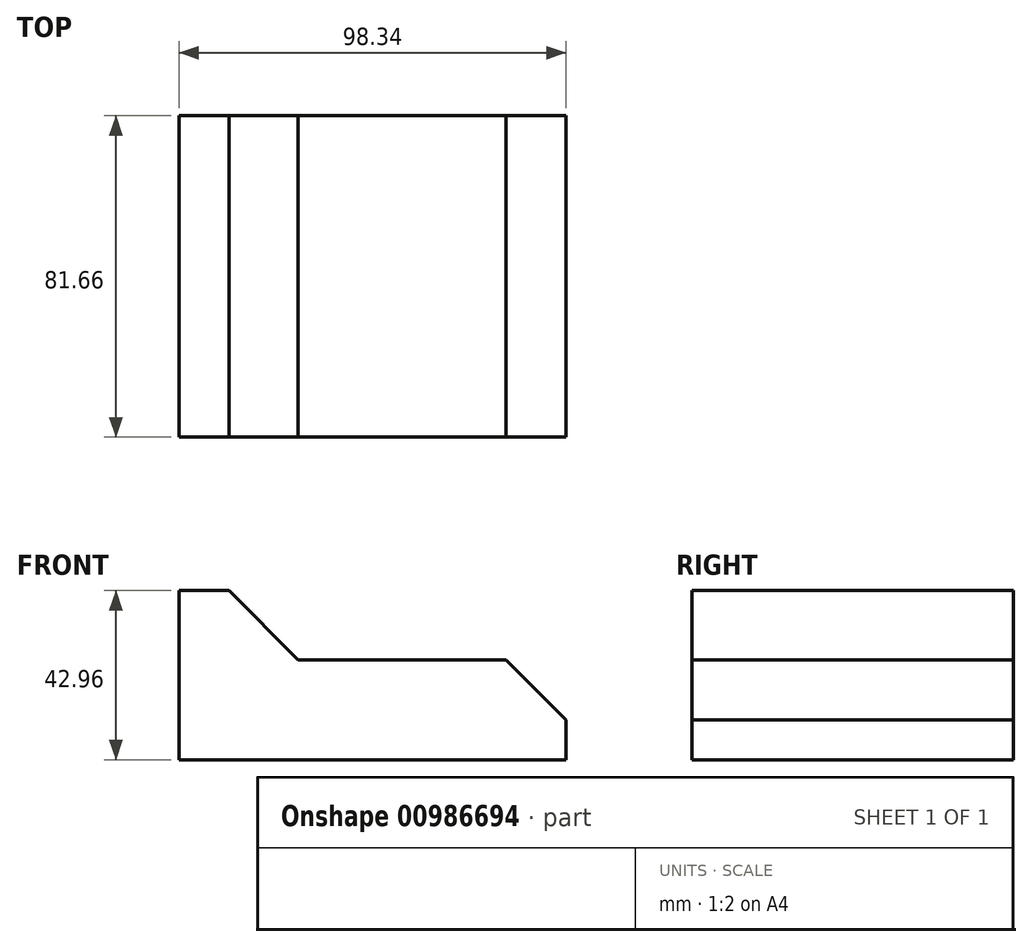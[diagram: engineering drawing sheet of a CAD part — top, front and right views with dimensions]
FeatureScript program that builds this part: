
annotation { "Feature Type Name" : "Feature", "Feature Type Description" : "" }
export const myFeature = defineFeature(function(context is Context, id is Id, definition is map)
    precondition{}
    {
        {
            var Q0;
            Q0=qCreatedBy(makeId("Top.planeOp"),FACE);
            var sketch = newSketch(context, id + "F0", { "sketchPlane" : qUnion([Q0])});
            skLineSegment(sketch, "E0.bottom", {"start": v(0, -23.3) * mm, "end": v(41.38, -23.3) * mm});
            skLineSegment(sketch, "E0.top", {"start": v(0, 20.26) * mm, "end": v(41.38, 20.26) * mm});
            skLineSegment(sketch, "E0.left", {"start": v(0, -23.3) * mm, "end": v(0, 20.26) * mm});
            skLineSegment(sketch, "E0.right", {"start": v(41.38, -23.3) * mm, "end": v(41.38, 20.26) * mm});
            skLineSegment(sketch, "E1.bottom", {"start": v(41.38, 20.26) * mm, "end": v(70.31, 20.26) * mm});
            skLineSegment(sketch, "E1.top", {"start": v(41.38, -23.3) * mm, "end": v(70.31, -23.3) * mm});
            skLineSegment(sketch, "E1.left", {"start": v(41.38, 20.26) * mm, "end": v(41.38, -23.3) * mm});
            skLineSegment(sketch, "E1.right", {"start": v(70.31, 20.26) * mm, "end": v(70.31, -23.3) * mm});
            skLineSegment(sketch, "E2.bottom", {"start": v(0, 20.26) * mm, "end": v(-15.33, 20.26) * mm});
            skLineSegment(sketch, "E2.top", {"start": v(0, -23.3) * mm, "end": v(-15.33, -23.3) * mm});
            skLineSegment(sketch, "E2.left", {"start": v(0, 20.26) * mm, "end": v(0, -23.3) * mm});
            skLineSegment(sketch, "E2.right", {"start": v(-15.33, 20.26) * mm, "end": v(-15.33, -23.3) * mm});
            skSolve(sketch);
        }
        {
            var Q0;
            Q0=makeQuery(id+"F0.imprint","IMPRINT",FACE,{"disambiguationData":[TD([[makeQuery(id+"F0.imprint","IMPRINT",EDGE,{"derivedFrom":sQuery(id+"F0.wireOp",EDGE,"E2.bottom")}),1.0]])]});
            var Q1;
            Q1=makeQuery(id+"F0.imprint","IMPRINT",FACE,{"disambiguationData":[TD([[makeQuery(id+"F0.imprint","IMPRINT",EDGE,{"derivedFrom":sQuery(id+"F0.wireOp",EDGE,"E0.bottom")}),1.0]])]});
            var Q2;
            Q2=makeQuery(id+"F0.imprint","IMPRINT",FACE,{"disambiguationData":[TD([[makeQuery(id+"F0.imprint","IMPRINT",EDGE,{"derivedFrom":sQuery(id+"F0.wireOp",EDGE,"E1.bottom")}),-1.0]])]});
            extrude(context, id + "F1", {"entities" : qUnion([Q0, Q1, Q2]), "depth" : 25.4 * mm, "offsetDistance" : 25.4 * mm});
        }
        {
            var Q0;
            Q0=makeQuery(id+"F1.opExtrude","CAP_FACE",FACE,{"disambiguationData":[OSD([sQuery(id+"F0.wireOp",EDGE,"E0.bottom"),sQuery(id+"F0.wireOp",EDGE,"E0.top"),sQuery(id+"F0.wireOp",EDGE,"E1.bottom"),sQuery(id+"F0.wireOp",EDGE,"E1.top"),sQuery(id+"F0.wireOp",EDGE,"E1.right"),sQuery(id+"F0.wireOp",EDGE,"E2.bottom"),sQuery(id+"F0.wireOp",EDGE,"E2.top"),sQuery(id+"F0.wireOp",EDGE,"E2.right")])],"isStart":false});
            var sketch = newSketch(context, id + "F2", { "sketchPlane" : qUnion([Q0])});
            skLineSegment(sketch, "E3.bottom", {"start": v(-15.33, 20.26) * mm, "end": v(2.23, 20.26) * mm});
            skLineSegment(sketch, "E3.top", {"start": v(-15.33, -23.3) * mm, "end": v(2.23, -23.3) * mm});
            skLineSegment(sketch, "E3.left", {"start": v(-15.33, 20.26) * mm, "end": v(-15.33, -23.3) * mm});
            skLineSegment(sketch, "E3.right", {"start": v(2.23, 20.26) * mm, "end": v(2.23, -23.3) * mm});
            skLineSegment(sketch, "E4.bottom", {"start": v(51.88, 20.26) * mm, "end": v(70.31, 20.26) * mm});
            skLineSegment(sketch, "E4.top", {"start": v(51.88, -23.3) * mm, "end": v(70.31, -23.3) * mm});
            skLineSegment(sketch, "E4.left", {"start": v(51.88, 20.26) * mm, "end": v(51.88, -23.3) * mm});
            skLineSegment(sketch, "E4.right", {"start": v(70.31, 20.26) * mm, "end": v(70.31, -23.3) * mm});
            skSolve(sketch);
        }
        {
            var Q0;
            Q0=makeQuery(id+"F2.imprint","IMPRINT",FACE,{"disambiguationData":[TD([[makeQuery(id+"F2.imprint","IMPRINT",EDGE,{"derivedFrom":sQuery(id+"F2.wireOp",EDGE,"E3.bottom")}),1.0]])]});
            extrude(context, id + "F3", {"entities" : qUnion([Q0]), "operationType" : NewBodyOperationType.ADD, "depth" : 25.4 * mm, "offsetDistance" : 25.4 * mm});
        }
        {
            var Q0;
            Q0=makeQuery(id+"F1.opExtrude","CAP_EDGE",EDGE,{"disambiguationData":[OSD([sQuery(id+"F0.wireOp",EDGE,"E1.right")])],"isStart":false});
            chamfer(context, id + "F4", {"entities" : qUnion([Q0]), "width" : 15.24 * mm, "tangentPropagation" : true});
        }
        {
            var Q0;
            Q0=makeQuery(id+"F3.opExtrude","CAP_EDGE",EDGE,{"disambiguationData":[OSD([sQuery(id+"F2.wireOp",EDGE,"E3.right")])],"isStart":false});
            chamfer(context, id + "F5", {"entities" : qUnion([Q0]), "width" : 25.4 * mm, "tangentPropagation" : true});
        }
        {
            var Q0;
            Q0=makeQuery(id+"F3.boolean.opBoolean","MERGE",FACE,{"derivedFrom":[makeQuery(id+"F1.opExtrude","SWEPT_FACE",FACE,{"disambiguationData":[OSD([sQuery(id+"F0.wireOp",EDGE,"E2.right")])]}),makeQuery(id+"F3.opExtrude","SWEPT_FACE",FACE,{"disambiguationData":[OSD([sQuery(id+"F2.wireOp",EDGE,"E3.left")])]})]});
            extrude(context, id + "F6", {"entities" : qUnion([Q0]), "operationType" : NewBodyOperationType.ADD, "depth" : 12.7 * mm, "offsetDistance" : 25.4 * mm});
        }
        {
            var Q0;
            {var subQ0=sQuery(id+"F2.wireOp",EDGE,"E3.bottom");var subQ1=sQuery(id+"F0.wireOp",EDGE,"E2.bottom");Q0=makeQuery(id+"F6.boolean.opBoolean","MERGE",FACE,{"derivedFrom":[makeQuery(id+"F3.boolean.opBoolean","MERGE",FACE,{"derivedFrom":[makeQuery(id+"F1.opExtrude","SWEPT_FACE",FACE,{"disambiguationData":[OSD([sQuery(id+"F0.wireOp",EDGE,"E0.top"),sQuery(id+"F0.wireOp",EDGE,"E1.bottom"),subQ1])]}),makeQuery(id+"F3.opExtrude","SWEPT_FACE",FACE,{"disambiguationData":[OSD([subQ0])]})]}),makeQuery(id+"F6.opExtrude","SWEPT_FACE",FACE,{"disambiguationData":[OSD([subQ1,sQuery(id+"F0.wireOp",EDGE,"E2.right"),subQ0,sQuery(id+"F2.wireOp",EDGE,"E3.left")])]})]});}
            extrude(context, id + "F7", {"entities" : qUnion([Q0]), "operationType" : NewBodyOperationType.ADD, "depth" : 25.4 * mm, "offsetDistance" : 25.4 * mm});
        }
        {
            var Q0;
            Q0=makeQuery(id+"F7.opExtrude","CAP_FACE",FACE,{"disambiguationData":[OSD([sQuery(id+"F0.wireOp",EDGE,"E0.top"),sQuery(id+"F0.wireOp",EDGE,"E1.bottom"),sQuery(id+"F0.wireOp",EDGE,"E2.bottom"),sQuery(id+"F0.wireOp",EDGE,"E2.right"),sQuery(id+"F2.wireOp",EDGE,"E3.bottom"),sQuery(id+"F2.wireOp",EDGE,"E3.left")])],"isStart":false});
            extrude(context, id + "F8", {"entities" : qUnion([Q0]), "operationType" : NewBodyOperationType.ADD, "depth" : 12.7 * mm, "offsetDistance" : 25.4 * mm});
        }
    });
